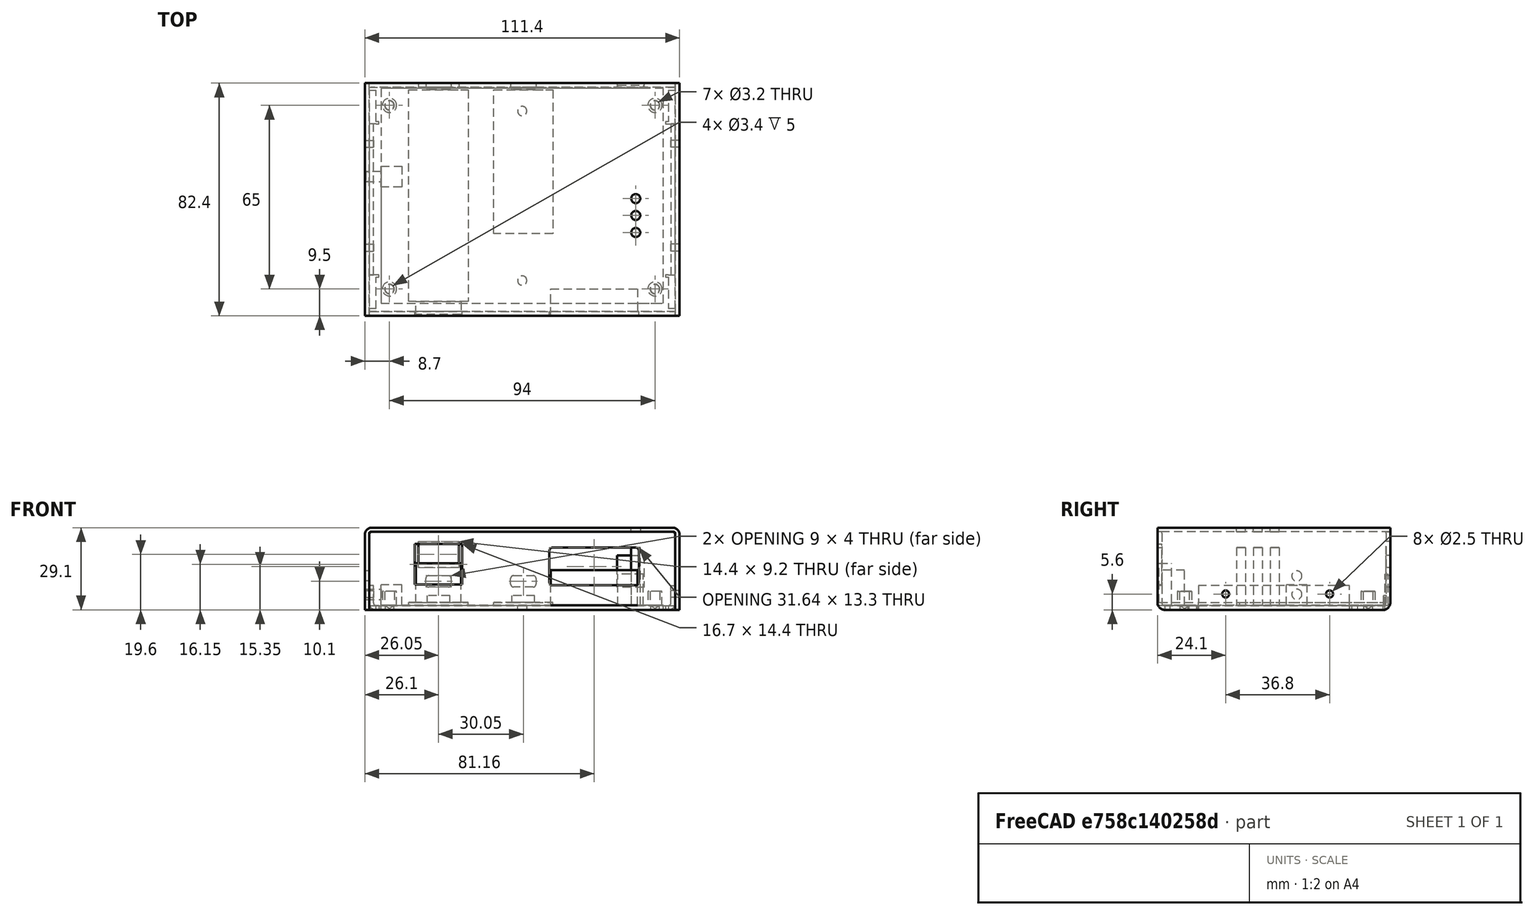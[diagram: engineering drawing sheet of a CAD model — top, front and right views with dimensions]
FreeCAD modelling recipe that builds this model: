
FCSTD DOCUMENT  (FreeCAD 0.21R33110 (Git))
Label: winners-case-v2-front
License: All rights reserved
LicenseURL: http://en.wikipedia.org/wiki/All_rights_reserved
objects: Sketcher::SketchObject×23, TechDraw::DrawViewPart×17, PartDesign::Pad×14, PartDesign::FeaturePython×6, PartDesign::Hole×6, TechDraw::DrawSVGTemplate×6, TechDraw::DrawPage×6, PartDesign::Fillet×4, TechDraw::DrawViewDimension×4, PartDesign::Body×3, App::Part×3, PartDesign::Pocket×3, Spreadsheet::Sheet×1
note: 94 computed .brp shape members not serialized (recipe doc carries the construction recipe); baked Part::Feature solids carry a one-line shape summary decoded from their .brp

FEATURE [Sketcher::SketchObject] Sketch
  FullyConstrained = true
  MapMode = 5
  Support = -> [XY_Plane]
  expr: .Constraints.pcb_h = <<fig>>.pcb_h
  expr: .Constraints.pcb_hole_bottom = <<fig>>.pcb_hole_bottom
  expr: .Constraints.pcb_hole_left = <<fig>>.pcb_hole_left
  expr: .Constraints.pcb_hole_r = <<fig>>.pcb_hole_r
  expr: .Constraints.pcb_hole_right = <<fig>>.pcb_hole_right
  expr: .Constraints.pcb_hole_top = <<fig>>.pcb_hole_top
  expr: .Constraints.pcb_w = <<fig>>.pcb_w
  sketch-geometry (9):
    g0: LineSegment StartX=50 StartY=-38 StartZ=0 EndX=50 EndY=38 EndZ=0
    g1: LineSegment StartX=50 StartY=38 StartZ=0 EndX=-50 EndY=38 EndZ=0
    g2: LineSegment StartX=-50 StartY=38 StartZ=0 EndX=-50 EndY=-38 EndZ=0
    g3: LineSegment StartX=-50 StartY=-38 StartZ=0 EndX=50 EndY=-38 EndZ=0
    g4: GeomPoint X=0 Y=0 Z=0
    g5: Circle CenterX=-47 CenterY=32 CenterZ=0 NormalX=0 NormalY=0 NormalZ=1 AngleXU=0 Radius=1.6
    g6: Circle CenterX=47 CenterY=32 CenterZ=0 NormalX=0 NormalY=0 NormalZ=1 AngleXU=0 Radius=1.6
    g7: Circle CenterX=-47 CenterY=-33 CenterZ=0 NormalX=0 NormalY=0 NormalZ=1 AngleXU=0 Radius=1.6
    g8: Circle CenterX=47 CenterY=-33 CenterZ=0 NormalX=0 NormalY=0 NormalZ=1 AngleXU=0 Radius=1.6
  constraints (24):
    c: Coincident(g0,g1)
    c: Coincident(g1,g2)
    c: Coincident(g2,g3)
    c: Coincident(g3,g0)
    c: Horizontal(g1)
    c: Horizontal(g3)
    c: Vertical(g0)
    c: Vertical(g2)
    c: Symmetric(g1,g0,g4)
    c: Coincident(g4,g-1)
    c: DistanceX(g1,g1) = 100  'pcb_w'
    c: DistanceY(g0,g0) = 76  'pcb_h'
    c: Radius(g5) = 1.6  'pcb_hole_r'
    c: Equal(g5,g6)
    c: Equal(g6,g8)
    c: Equal(g8,g7)
    c: DistanceX(g1,g5) = 3  'pcb_hole_left'
    c: DistanceY(g5,g1) = 6  'pcb_hole_top'
    c: DistanceX(g6,g0) = 3  'pcb_hole_right'
    c: DistanceY(g2,g7) = 5  'pcb_hole_bottom'
    c: Horizontal(g6,g5)
    c: Vertical(g5,g7)
    c: Vertical(g6,g8)
    c: Horizontal(g7,g8)
FEATURE [Spreadsheet::Sheet] Spreadsheet  label="fig"
  cells = A1=margin2; B1(margin2)=0.2; A2=margin; B2(margin)=0.4; A3=pcb_surface_z; B3(pcb_surface_z)==sheet_thk + standoff_h + pcb_thk; A4=pcb_w; B4(pcb_w)=100; A5=pcb_w2; B5(pcb_w2)=50; A6=pcb_h; B6(pcb_h)=76; A7=pcb_h2; B7(pcb_h2)==76 / 2; A8=pcb_thk; B8(pcb_thk)=1.6; A9=pcb_hole_left; B9(pcb_hole_left)=3; A10=pcb_hole_right; B10(pcb_hole_right)=3; A11=pcb_hole_top; B11(pcb_hole_top)=6; A12=pcb_hole_bottom; B12(pcb_hole_bottom)=5; A13=pcb_hole_r; B13(pcb_hole_r)=1.6; A14=standoff_h; B14(standoff_h)=5; A15=standoff_tab_r; B15(standoff_tab_r)=1.6; A16=standoff_r; B16(standoff_r)=2.5; A17=rj45_w; B17(rj45_w)=15.9; A18=rj45_h; B18(rj45_h)=13.6; A19=rj45_bottom_margin; B19(rj45_bottom_margin)=0.25; A20=rj45_y_ext; B20(rj45_y_ext)=4.5; A21=w5500_top; B21(w5500_top)=0.48; A22=w5500_left; B22(w5500_left)=9.85; A23=w5500_h; B23(w5500_h)=75; A24=w5500_w; B24(w5500_w)=21; A25=w5500_thk; B25(w5500_thk)=1; A26=pico_left; B26(pico_left)=39.9; A27=pico_h; B27(pico_h)=51; A28=pico_w; B28(pico_w)=21; A29=usb_w; B29(usb_w)=8; A30=usb_h; B30(usb_h)=3; A31=usb_bottom_margin; B31(usb_bottom_margin)=-0.5; A32=usb_margin; B32(usb_margin)=0.5; A33=usb_ext; B33(usb_ext)=1; A34=db9_w; B34(db9_w)=30.84; A35=db9_h; B35(db9_h)=12.5; A36=db9_support_to_face; B36(db9_support_to_face)=9.52; A37=db9_support_dist; B37(db9_support_dist)=25; A38=db9_support_to_side; B38(db9_support_to_side)=2.92; A39=db9_left; B39(db9_left)=62.96; A40=db9_bottom; B40(db9_bottom)=5.07; A41=db9_right; B41(db9_right)=12.14; A42=barrel_w; B42(barrel_w)=9; A43=barrel_h; B43(barrel_h)=11; A44=barrel_ext; B44(barrel_ext)=1.1; A45=barrel_bottom_margin; B45(barrel_bottom_margin)=-0.2; A46=barrel_support_to_face; B46(barrel_support_to_face)=0; A47=barrel_right; B47(barrel_right)=7.15; A48=pb_h; B48(pb_h)=7.4; A49=pb_w; B49(pb_w)=7.4; A50=pb_tall; B50(pb_tall)=7.2; A51=pb_r; B51(pb_r)==3.6 / 2; A52=pb_center_y; B52(pb_center_y)=31.2; A53=pb_top; B53(pb_top)==pb_center_y - pb_h / 2; A54=pb_ext; B54(pb_ext)=5.4; A55=pb_bottom_margin; B55(pb_bottom_margin)=0.3; A56=led_r; B56(led_r)==3.2 / 2; A57=led1_bottom; B57(led1_bottom)=37; A58=led2_bottom; B58(led2_bottom)=31; A59=led3_bottom; B59(led3_bottom)=25; A60=led_right; B60(led_right)=9.8; A61=led_tall; B61(led_tall)=20.5; A62=led_dist; B62(led_dist)=6; A63=sheet_thk; B63(sheet_thk)=1.5; A64=sheet_base_w2; B64(sheet_base_w2)==pcb_w2 + pb_ext - sheet_thk * 0.8; A65=sheet_h2_top; B65(sheet_h2_top)==pcb_h2 + margin; A66=sheet_h2_bottom; B66(sheet_h2_bottom)==pcb_h2 + rj45_y_ext - sheet_thk; A67=sheet_bend_tall; B67(sheet_bend_tall)==sheet_thk + standoff_h + pcb_thk + led_tall - sheet_thk + sheet_bend_add; A68=sheet_bend_add; B68(sheet_bend_add)=2; A69=sheet_wing2wall; B69(sheet_wing2wall)=12; A70=sheet_wing_h; B70(sheet_wing_h)==sheet_thk + pcb_thk + standoff_h; A71=sheet_wing_hole_top; B71(sheet_wing_hole_top)=2.5; A72=sheetwing_hole_dist; B72(sheet_wing_hole_left)=18.4; A73=rsw_w; B73(rsw_w)=14.4; A74=rsw_h; B74(rsw_h)=9.2; A75=sheetwing_hole_top; B75(sheetwing_hole_top)=2.5; A76=sheet_wing_hole_dist; B76(sheet_wing_hole_dist)=18.4; A77=sheettop_bend_tall; B77(sheettop_bend_tall)==sheet_bend_tall - sheet_bend_add - 0.5; A78=sheet_dinrail_hole_dist; B78(sheet_dinrail_hole_dist)=30
FEATURE [PartDesign::Pad] Pad  label="pcb"
  Direction = (0,0,1)
  Length = 1.6
  Length2 = 10
  Profile = -> Sketch
  ReferenceAxis = -> Sketch [N_Axis]
  Type = 0
  expr: Length = <<fig>>.pcb_thk
FEATURE [Sketcher::SketchObject] Sketch001
  AttachmentOffset = pos=(0,0,1.6) rot=(0,0,1;0rad)
  FullyConstrained = true
  MapMode = 5
  Placement = pos=(0,0,1.6) rot=(0,0,1;0rad)
  Support = -> [XY_Plane]
  expr: .AttachmentOffset.Base.z = <<fig>>.pcb_thk
  expr: .Constraints.w5500_h = <<fig>>.w5500_h
  expr: Constraints[10] = <<fig>>.pcb_w / 2 - <<fig>>.w5500_left
  expr: Constraints[11] = <<fig>>.pcb_h / 2 - 0.48
  expr: Constraints[8] = <<fig>>.w5500_w
  sketch-geometry (4):
    g0: LineSegment StartX=-40.15 StartY=37.52 StartZ=0 EndX=-19.15 EndY=37.52 EndZ=0
    g1: LineSegment StartX=-19.15 StartY=37.52 StartZ=0 EndX=-19.15 EndY=-37.48 EndZ=0
    g2: LineSegment StartX=-19.15 StartY=-37.48 StartZ=0 EndX=-40.15 EndY=-37.48 EndZ=0
    g3: LineSegment StartX=-40.15 StartY=-37.48 StartZ=0 EndX=-40.15 EndY=37.52 EndZ=0
  constraints (12):
    c: Coincident(g0,g1)
    c: Coincident(g1,g2)
    c: Coincident(g2,g3)
    c: Coincident(g3,g0)
    c: Horizontal(g0)
    c: Horizontal(g2)
    c: Vertical(g1)
    c: Vertical(g3)
    c: DistanceX(g2,g2) = 21
    c: DistanceY(g1,g1) = 75  'w5500_h'
    c: DistanceX(g0,g-1) = 40.15
    c: DistanceY(g-1,g0) = 37.52
FEATURE [PartDesign::Pad] Pad001  label="w5500-pcb"
  BaseFeature = -> Pad
  Direction = (0,0,1)
  Length = 1
  Length2 = 10
  Profile = -> Sketch001
  ReferenceAxis = -> Sketch001 [N_Axis]
  Type = 0
  expr: Length = <<fig>>.w5500_thk
FEATURE [Sketcher::SketchObject] Sketch002
  AttachmentOffset = pos=(0,0,2.59) rot=(0,0,1;0rad)
  FullyConstrained = true
  MapMode = 5
  Placement = pos=(0,0,2.59) rot=(0,0,1;0rad)
  Support = -> [XY_Plane]
  expr: .AttachmentOffset.Base.z = <<fig>>.pcb_thk + <<fig>>.w5500_thk - 0.01
  expr: .Constraints.rj45_w = <<fig>>.rj45_w
  expr: Constraints[10] = <<fig>>.w5500_top + <<fig>>.w5500_h - <<fig>>.pcb_h / 2
  expr: Constraints[11] = <<fig>>.pcb_w / 2 - <<fig>>.w5500_left - <<fig>>.w5500_w + (<<fig>>.w5500_w - <<fig>>.rj45_w) / 2
  expr: Constraints[9] = <<fig>>.rj45_y_ext
  sketch-geometry (4):
    g0: LineSegment StartX=-37.6 StartY=-37.48 StartZ=0 EndX=-21.7 EndY=-37.48 EndZ=0
    g1: LineSegment StartX=-21.7 StartY=-37.48 StartZ=0 EndX=-21.7 EndY=-41.98 EndZ=0
    g2: LineSegment StartX=-21.7 StartY=-41.98 StartZ=0 EndX=-37.6 EndY=-41.98 EndZ=0
    g3: LineSegment StartX=-37.6 StartY=-41.98 StartZ=0 EndX=-37.6 EndY=-37.48 EndZ=0
  constraints (12):
    c: Coincident(g0,g1)
    c: Coincident(g1,g2)
    c: Coincident(g2,g3)
    c: Coincident(g3,g0)
    c: Horizontal(g0)
    c: Horizontal(g2)
    c: Vertical(g1)
    c: Vertical(g3)
    c: DistanceX(g0,g0) = 15.9  'rj45_w'
    c: DistanceY(g1,g1) = 4.5
    c: DistanceY(g0,g-1) = 37.48
    c: DistanceX(g0,g-1) = 21.7
FEATURE [PartDesign::Pad] Pad002  label="w5500-rj45"
  BaseFeature = -> Pad001
  Direction = (0,0,1)
  Length = 13.85
  Length2 = 10
  Profile = -> Sketch002
  ReferenceAxis = -> Sketch002 [N_Axis]
  Type = 0
  expr: Length = <<fig>>.rj45_bottom_margin + <<fig>>.rj45_h
FEATURE [Sketcher::SketchObject] Sketch003
  AttachmentOffset = pos=(0,0,2.599) rot=(0,0,1;0rad)
  FullyConstrained = true
  MapMode = 5
  Placement = pos=(0,0,2.599) rot=(0,0,1;0rad)
  Support = -> [XY_Plane]
  expr: .AttachmentOffset.Base.z = <<fig>>.pcb_thk + <<fig>>.w5500_thk - 0.001
  expr: Constraints[10] = <<fig>>.pcb_w / 2 - <<fig>>.w5500_left - (<<fig>>.w5500_w - <<fig>>.usb_w) / 2
  expr: Constraints[11] = <<fig>>.pcb_h / 2 - <<fig>>.w5500_top
  expr: Constraints[8] = <<fig>>.usb_ext
  expr: Constraints[9] = <<fig>>.usb_w
  sketch-geometry (4):
    g0: LineSegment StartX=-33.65 StartY=38.52 StartZ=0 EndX=-25.65 EndY=38.52 EndZ=0
    g1: LineSegment StartX=-25.65 StartY=38.52 StartZ=0 EndX=-25.65 EndY=37.52 EndZ=0
    g2: LineSegment StartX=-25.65 StartY=37.52 StartZ=0 EndX=-33.65 EndY=37.52 EndZ=0
    g3: LineSegment StartX=-33.65 StartY=37.52 StartZ=0 EndX=-33.65 EndY=38.52 EndZ=0
  constraints (12):
    c: Coincident(g0,g1)
    c: Coincident(g1,g2)
    c: Coincident(g2,g3)
    c: Coincident(g3,g0)
    c: Horizontal(g0)
    c: Horizontal(g2)
    c: Vertical(g1)
    c: Vertical(g3)
    c: DistanceY(g1,g1) = 1
    c: DistanceX(g2,g2) = 8
    c: DistanceX(g2,g-1) = 33.65
    c: DistanceY(g-1,g1) = 37.52
FEATURE [PartDesign::Pad] Pad003  label="w5500-usb"
  BaseFeature = -> Pad002
  Direction = (0,0,1)
  Length = 2.5
  Length2 = 10
  Profile = -> Sketch003
  ReferenceAxis = -> Sketch003 [N_Axis]
  Type = 0
  expr: Length = <<fig>>.usb_bottom_margin + <<fig>>.usb_h
FEATURE [Sketcher::SketchObject] Sketch004
  AttachmentOffset = pos=(0,0,1.6) rot=(0,0,1;0rad)
  FullyConstrained = true
  MapMode = 5
  Placement = pos=(0,0,1.6) rot=(0,0,1;0rad)
  Support = -> [XY_Plane]
  expr: .AttachmentOffset.Base.z = <<fig>>.pcb_thk
  expr: Constraints[10] = <<fig>>.db9_left - <<fig>>.db9_support_to_side - <<fig>>.pcb_w / 2
  expr: Constraints[11] = <<fig>>.pcb_h / 2 - <<fig>>.db9_bottom
  expr: Constraints[8] = <<fig>>.db9_w
  expr: Constraints[9] = <<fig>>.db9_support_to_face
  sketch-geometry (4):
    g0: LineSegment StartX=10.04 StartY=-32.93 StartZ=0 EndX=40.88 EndY=-32.93 EndZ=0
    g1: LineSegment StartX=40.88 StartY=-32.93 StartZ=0 EndX=40.88 EndY=-42.45 EndZ=0
    g2: LineSegment StartX=40.88 StartY=-42.45 StartZ=0 EndX=10.04 EndY=-42.45 EndZ=0
    g3: LineSegment StartX=10.04 StartY=-42.45 StartZ=0 EndX=10.04 EndY=-32.93 EndZ=0
  constraints (12):
    c: Coincident(g0,g1)
    c: Coincident(g1,g2)
    c: Coincident(g2,g3)
    c: Coincident(g3,g0)
    c: Horizontal(g0)
    c: Horizontal(g2)
    c: Vertical(g1)
    c: Vertical(g3)
    c: DistanceX(g0,g0) = 30.84
    c: DistanceY(g3,g3) = 9.52
    c: DistanceX(g-1,g0) = 10.04
    c: DistanceY(g0,g-1) = 32.93
FEATURE [PartDesign::Pad] Pad004  label="DB9"
  BaseFeature = -> Pad003
  Direction = (0,0,1)
  Length = 12.5
  Length2 = 10
  Profile = -> Sketch004
  ReferenceAxis = -> Sketch004 [N_Axis]
  Type = 0
  expr: Length = <<fig>>.db9_h
FEATURE [Sketcher::SketchObject] Sketch005
  AttachmentOffset = pos=(0,0,1.6) rot=(0,0,1;0rad)
  FullyConstrained = true
  MapMode = 5
  Placement = pos=(0,0,1.6) rot=(0,0,1;0rad)
  Support = -> [XY_Plane]
  expr: .AttachmentOffset.Base.z = <<fig>>.pcb_thk
  expr: Constraints[10] = <<fig>>.pcb_h / 2 - <<fig>>.w5500_top
  expr: Constraints[11] = <<fig>>.pcb_w / 2 - <<fig>>.pico_left
  expr: Constraints[8] = <<fig>>.pico_w
  expr: Constraints[9] = <<fig>>.pico_h
  sketch-geometry (4):
    g0: LineSegment StartX=-10.1 StartY=37.52 StartZ=0 EndX=10.9 EndY=37.52 EndZ=0
    g1: LineSegment StartX=10.9 StartY=37.52 StartZ=0 EndX=10.9 EndY=-13.48 EndZ=0
    g2: LineSegment StartX=10.9 StartY=-13.48 StartZ=0 EndX=-10.1 EndY=-13.48 EndZ=0
    g3: LineSegment StartX=-10.1 StartY=-13.48 StartZ=0 EndX=-10.1 EndY=37.52 EndZ=0
  constraints (12):
    c: Coincident(g0,g1)
    c: Coincident(g1,g2)
    c: Coincident(g2,g3)
    c: Coincident(g3,g0)
    c: Horizontal(g0)
    c: Horizontal(g2)
    c: Vertical(g1)
    c: Vertical(g3)
    c: DistanceX(g0,g0) = 21
    c: DistanceY(g3,g3) = 51
    c: DistanceY(g-1,g0) = 37.52
    c: DistanceX(g0,g-1) = 10.1
FEATURE [PartDesign::Pad] Pad005  label="pico-pcb"
  BaseFeature = -> Pad004
  Direction = (0,0,1)
  Length = 1
  Length2 = 10
  Profile = -> Sketch005
  ReferenceAxis = -> Sketch005 [N_Axis]
  Type = 0
  expr: Length = <<fig>>.w5500_thk
FEATURE [Sketcher::SketchObject] Sketch006
  AttachmentOffset = pos=(0,0,2.599) rot=(0,0,1;0rad)
  FullyConstrained = true
  MapMode = 5
  Placement = pos=(0,0,2.599) rot=(0,0,1;0rad)
  Support = -> [XY_Plane]
  expr: .AttachmentOffset.Base.z = <<fig>>.pcb_thk + <<fig>>.w5500_thk - 0.001
  expr: Constraints[10] = <<fig>>.pcb_w / 2 - <<fig>>.pico_left - (<<fig>>.pico_w - <<fig>>.usb_w) / 2
  expr: Constraints[11] = <<fig>>.pcb_h / 2 - <<fig>>.w5500_top
  expr: Constraints[8] = <<fig>>.usb_w
  expr: Constraints[9] = <<fig>>.usb_ext
  sketch-geometry (4):
    g0: LineSegment StartX=-3.6 StartY=38.52 StartZ=0 EndX=4.4 EndY=38.52 EndZ=0
    g1: LineSegment StartX=4.4 StartY=38.52 StartZ=0 EndX=4.4 EndY=37.52 EndZ=0
    g2: LineSegment StartX=4.4 StartY=37.52 StartZ=0 EndX=-3.6 EndY=37.52 EndZ=0
    g3: LineSegment StartX=-3.6 StartY=37.52 StartZ=0 EndX=-3.6 EndY=38.52 EndZ=0
  constraints (12):
    c: Coincident(g0,g1)
    c: Coincident(g1,g2)
    c: Coincident(g2,g3)
    c: Coincident(g3,g0)
    c: Horizontal(g0)
    c: Horizontal(g2)
    c: Vertical(g1)
    c: Vertical(g3)
    c: DistanceX(g0,g0) = 8
    c: DistanceY(g1,g1) = 1
    c: DistanceX(g2,g-1) = 3.6
    c: DistanceY(g-1,g2) = 37.52
FEATURE [PartDesign::Pad] Pad006  label="pico-usb"
  BaseFeature = -> Pad005
  Direction = (0,0,1)
  Length = 2.5
  Length2 = 10
  Profile = -> Sketch006
  ReferenceAxis = -> Sketch006 [N_Axis]
  Type = 0
  expr: Length = <<fig>>.usb_bottom_margin + <<fig>>.usb_h
FEATURE [Sketcher::SketchObject] Sketch007
  AttachmentOffset = pos=(0,0,1.599) rot=(0,0,1;0rad)
  FullyConstrained = true
  MapMode = 5
  Placement = pos=(0,0,1.599) rot=(0,0,1;0rad)
  Support = -> [XY_Plane]
  expr: .AttachmentOffset.Base.z = <<fig>>.pcb_thk - 0.001
  expr: Constraints[10] = <<fig>>.pcb_w / 2 - <<fig>>.barrel_right - <<fig>>.barrel_w
  expr: Constraints[11] = <<fig>>.pcb_h / 2
  expr: Constraints[8] = <<fig>>.barrel_w
  expr: Constraints[9] = <<fig>>.barrel_ext
  sketch-geometry (4):
    g0: LineSegment StartX=33.85 StartY=39.1 StartZ=0 EndX=42.85 EndY=39.1 EndZ=0
    g1: LineSegment StartX=42.85 StartY=39.1 StartZ=0 EndX=42.85 EndY=38 EndZ=0
    g2: LineSegment StartX=42.85 StartY=38 StartZ=0 EndX=33.85 EndY=38 EndZ=0
    g3: LineSegment StartX=33.85 StartY=38 StartZ=0 EndX=33.85 EndY=39.1 EndZ=0
  constraints (12):
    c: Coincident(g0,g1)
    c: Coincident(g1,g2)
    c: Coincident(g2,g3)
    c: Coincident(g3,g0)
    c: Horizontal(g0)
    c: Horizontal(g2)
    c: Vertical(g1)
    c: Vertical(g3)
    c: DistanceX(g0,g0) = 9
    c: DistanceY(g3,g3) = 1.1
    c: DistanceX(g-1,g2) = 33.85
    c: DistanceY(g-1,g2) = 38
FEATURE [PartDesign::Pad] Pad007  label="barrel-jack"
  BaseFeature = -> Pad006
  Direction = (0,0,1)
  Length = 11
  Length2 = 10
  Profile = -> Sketch007
  ReferenceAxis = -> Sketch007 [N_Axis]
  Type = 0
  expr: Length = <<fig>>.barrel_h
FEATURE [Sketcher::SketchObject] Sketch008
  AttachmentOffset = pos=(0,0,1.6) rot=(0,0,1;0rad)
  FullyConstrained = true
  MapMode = 5
  Placement = pos=(0,0,1.6) rot=(0,0,1;0rad)
  Support = -> [XY_Plane]
  expr: .AttachmentOffset.Base.z = <<fig>>.pcb_thk
  expr: Constraints[10] = <<fig>>.pcb_h / 2 - <<fig>>.pb_top
  expr: Constraints[11] = <<fig>>.pcb_w / 2
  expr: Constraints[8] = <<fig>>.pb_w
  expr: Constraints[9] = <<fig>>.pb_h
  sketch-geometry (4):
    g0: LineSegment StartX=-50 StartY=10.5 StartZ=0 EndX=-42.6 EndY=10.5 EndZ=0
    g1: LineSegment StartX=-42.6 StartY=10.5 StartZ=0 EndX=-42.6 EndY=3.1 EndZ=0
    g2: LineSegment StartX=-42.6 StartY=3.1 StartZ=0 EndX=-50 EndY=3.1 EndZ=0
    g3: LineSegment StartX=-50 StartY=3.1 StartZ=0 EndX=-50 EndY=10.5 EndZ=0
  constraints (12):
    c: Coincident(g0,g1)
    c: Coincident(g1,g2)
    c: Coincident(g2,g3)
    c: Coincident(g3,g0)
    c: Horizontal(g0)
    c: Horizontal(g2)
    c: Vertical(g1)
    c: Vertical(g3)
    c: DistanceX(g0,g0) = 7.4
    c: DistanceY(g3,g3) = 7.4
    c: DistanceY(g-1,g0) = 10.5
    c: DistanceX(g2,g-1) = 50
FEATURE [PartDesign::Pad] Pad008  label="push-button"
  BaseFeature = -> Pad007
  Direction = (0,0,1)
  Length = 7.2
  Length2 = 10
  Profile = -> Sketch008
  ReferenceAxis = -> Sketch008 [N_Axis]
  Type = 0
  expr: Length = <<fig>>.pb_tall
FEATURE [Sketcher::SketchObject] Sketch009
  AttachmentOffset = pos=(0,0,-50) rot=(0,0,1;0rad)
  FullyConstrained = true
  MapMode = 5
  Placement = pos=(-50,1.11e-14,-1.11e-14) rot=(0.57735,0.57735,0.57735;2.0944rad)
  Support = -> [YZ_Plane]
  expr: .AttachmentOffset.Base.z = -<<fig>>.pcb_w2
  expr: Constraints[0] = <<fig>>.pb_r
  expr: Constraints[1] = <<fig>>.pcb_thk + <<fig>>.pb_tall / 2 + <<fig>>.pb_bottom_margin
  expr: Constraints[2] = <<fig>>.pcb_h2 - <<fig>>.pb_top - <<fig>>.pb_h / 2
  sketch-geometry (1):
    g0: Circle CenterX=6.8 CenterY=5.5 CenterZ=0 NormalX=0 NormalY=0 NormalZ=1 AngleXU=0 Radius=1.8
  constraints (3):
    c: Radius(g0) = 1.8
    c: DistanceY(g-1,g0) = 5.5
    c: DistanceX(g-1,g0) = 6.8
FEATURE [PartDesign::Pad] Pad009
  BaseFeature = -> Pad008
  Direction = (1,-2e-16,3e-16)
  Length = 5.4
  Length2 = 10
  Profile = -> Sketch009
  ReferenceAxis = -> Sketch009 [N_Axis]
  Reversed = true
  Type = 0
  expr: Length = <<fig>>.pb_ext
FEATURE [Sketcher::SketchObject] Sketch010
  AttachmentOffset = pos=(0,0,1.6) rot=(0,0,1;0rad)
  FullyConstrained = true
  MapMode = 5
  Placement = pos=(0,0,1.6) rot=(0,0,1;0rad)
  Support = -> [XY_Plane]
  expr: .AttachmentOffset.Base.z = <<fig>>.pcb_thk
  expr: Constraints[0] = <<fig>>.led_r
  expr: Constraints[3] = <<fig>>.pcb_w2 - <<fig>>.led_right
  expr: Constraints[6] = <<fig>>.pcb_h2 - <<fig>>.led1_bottom
  expr: Constraints[7] = <<fig>>.led_dist
  expr: Constraints[8] = <<fig>>.led_dist
  sketch-geometry (3):
    g0: Circle CenterX=40.2 CenterY=-1 CenterZ=0 NormalX=0 NormalY=0 NormalZ=1 AngleXU=0 Radius=1.6
    g1: Circle CenterX=40.2 CenterY=-7 CenterZ=0 NormalX=0 NormalY=0 NormalZ=1 AngleXU=0 Radius=1.6
    g2: Circle CenterX=40.2 CenterY=-13 CenterZ=0 NormalX=0 NormalY=0 NormalZ=1 AngleXU=0 Radius=1.6
  constraints (9):
    c: Radius(g0) = 1.6
    c: Equal(g0,g1)
    c: Equal(g1,g2)
    c: DistanceX(g-1,g0) = 40.2
    c: Vertical(g0,g1)
    c: Vertical(g1,g2)
    c: DistanceY(g0,g-1) = 1
    c: DistanceY(g1,g0) = 6
    c: DistanceY(g2,g1) = 6
FEATURE [PartDesign::Pad] Pad010
  BaseFeature = -> Pad009
  Direction = (0,0,1)
  Length = 20.5
  Length2 = 10
  Profile = -> Sketch010
  ReferenceAxis = -> Sketch010 [N_Axis]
  Type = 0
  expr: Length = <<fig>>.led_tall
FEATURE [PartDesign::Body] Body
  Group = -> [Sketch,Pad,Sketch001,Pad001,Sketch002,Pad002,Sketch003,Pad003,Sketch004,Pad004,Sketch005,Pad005,Sketch006,Pad006,Sketch007,Pad007,Sketch008,Pad008,Sketch009,Pad009,Sketch010,Pad010]
  Origin = -> Origin
  Tip = -> Pad010
FEATURE [App::Part] Part001  label="pcb2"
  Group = -> [Body]
  Origin = -> Origin002
  Placement = pos=(0,0,6.5) rot=(0,0,1;0rad)
  expr: .Placement.Base.z = <<fig>>.sheet_thk + <<fig>>.standoff_h
FEATURE [Sketcher::SketchObject] Sketch011
  FullyConstrained = true
  MapMode = 5
  Support = -> [XY_Plane004]
  expr: Constraints[10] = <<fig>>.pcb_h2 + <<fig>>.rj45_y_ext - <<fig>>.sheet_thk
  expr: Constraints[8] = <<fig>>.sheet_base_w2
  expr: Constraints[9] = <<fig>>.pcb_h2 + <<fig>>.margin
  sketch-geometry (5):
    g0: LineSegment StartX=54.2 StartY=-41 StartZ=0 EndX=54.2 EndY=38.4 EndZ=0
    g1: LineSegment StartX=54.2 StartY=38.4 StartZ=0 EndX=-54.2 EndY=38.4 EndZ=0
    g2: LineSegment StartX=-54.2 StartY=38.4 StartZ=0 EndX=-54.2 EndY=-41 EndZ=0
    g3: LineSegment StartX=-54.2 StartY=-41 StartZ=0 EndX=54.2 EndY=-41 EndZ=0
    g4: GeomPoint X=0 Y=0 Z=0
  constraints (12):
    c: Coincident(g0,g1)
    c: Coincident(g1,g2)
    c: Coincident(g2,g3)
    c: Coincident(g3,g0)
    c: Horizontal(g1)
    c: Vertical(g0)
    c: Vertical(g2)
    c: Coincident(g4,g-1)
    c: DistanceX(g1,g4) = 54.2
    c: DistanceY(g4,g1) = 38.4
    c: DistanceY(g2,g4) = 41
    c: Symmetric(g2,g0,g-2)
FEATURE [PartDesign::Pad] Pad011  label="base"
  Direction = (0,0,1)
  Length = 1.5
  Length2 = 10
  Profile = -> Sketch011
  ReferenceAxis = -> Sketch011 [N_Axis]
  Type = 0
  expr: Length = <<fig>>.sheet_thk
FEATURE [PartDesign::FeaturePython] Bend  # WARN: FeaturePython — macro-defined, semantics opaque (R4)
  AutoMiter = true
  BaseFeature = -> Pad011
  BendType = 2
  LengthList = [25.1]
  LengthSpec = 0
  ReliefFactor = 0.7
  UseReliefFactor = false
  angle = 90
  baseObject = -> Pad011 [Edge7]
  bendAList = [90]
  extend1 = 0
  extend2 = 0
  gap1 = 0
  gap2 = 0
  invert = true
  kfactor = 0.5
  length = 25.1
  maxExtendDist = 5
  minGap = 0.1
  minReliefGap = 1
  miterangle1 = 0
  miterangle2 = 0
  offset = 0
  radius = 1
  reliefType = 0
  reliefd = 1
  reliefw = 0.8
  sketchflip = false
  sketchinvert = false
  unfold = false
FEATURE [PartDesign::FeaturePython] Bend001  # WARN: FeaturePython — macro-defined, semantics opaque (R4)
  AutoMiter = true
  BaseFeature = -> Bend
  BendType = 2
  LengthList = [25.1]
  LengthSpec = 0
  ReliefFactor = 0.7
  UseReliefFactor = false
  angle = 90
  baseObject = -> Bend [Edge24]
  bendAList = [90]
  extend1 = 0
  extend2 = 0
  gap1 = 0
  gap2 = 0
  invert = true
  kfactor = 0.5
  length = 25.1
  maxExtendDist = 5
  minGap = 0.1
  minReliefGap = 1
  miterangle1 = 0
  miterangle2 = 0
  offset = 0
  radius = 1
  reliefType = 0
  reliefd = 1
  reliefw = 0.8
  sketchflip = false
  sketchinvert = false
  unfold = false
  expr: length = <<fig>>.sheet_thk + <<fig>>.standoff_h + <<fig>>.pcb_thk + <<fig>>.led_tall - <<fig>>.sheet_thk - <<fig>>.sheet_bend_add
FEATURE [Sketcher::SketchObject] Sketch012
  AttachmentOffset = pos=(0,0,44) rot=(0,0,1;0rad)
  FullyConstrained = true
  MapMode = 5
  Placement = pos=(0,-44,-9.8e-15) rot=(1,0,0;1.5708rad)
  Support = -> [XZ_Plane004]
  expr: .AttachmentOffset.Base.z = <<fig>>.pcb_h2 + <<fig>>.rj45_y_ext + <<fig>>.sheet_thk
  expr: Constraints[18] = <<fig>>.sheet_thk + <<fig>>.standoff_h + <<fig>>.pcb_thk + <<fig>>.w5500_thk - <<fig>>.margin
  expr: Constraints[19] = <<fig>>.db9_h + <<fig>>.margin * 2
  expr: Constraints[20] = <<fig>>.db9_w + <<fig>>.margin * 2
  expr: Constraints[21] = <<fig>>.db9_left - <<fig>>.db9_support_to_side - <<fig>>.pcb_w / 2 - <<fig>>.margin
  expr: Constraints[22] = <<fig>>.rj45_w + <<fig>>.margin * 2
  expr: Constraints[23] = <<fig>>.rj45_h + <<fig>>.margin * 2
  expr: Constraints[24] = <<fig>>.sheet_thk + <<fig>>.standoff_h + <<fig>>.pcb_thk + <<fig>>.rj45_bottom_margin + <<fig>>.w5500_thk - <<fig>>.margin
  expr: Constraints[25] = <<fig>>.pcb_w / 2 - <<fig>>.w5500_left - <<fig>>.w5500_w + (<<fig>>.w5500_w - <<fig>>.rj45_w) / 2 - <<fig>>.margin
  sketch-geometry (10):
    g0: LineSegment StartX=9.64 StartY=22 StartZ=0 EndX=9.64 EndY=8.7 EndZ=0
    g1: LineSegment StartX=9.64 StartY=8.7 StartZ=0 EndX=41.28 EndY=8.7 EndZ=0
    g2: LineSegment StartX=41.28 StartY=8.7 StartZ=0 EndX=41.28 EndY=22 EndZ=0
    g3: LineSegment StartX=41.28 StartY=22 StartZ=0 EndX=9.64 EndY=22 EndZ=0
    g4: GeomPoint X=25.46 Y=15.35 Z=0
    g5: LineSegment StartX=-38 StartY=23.35 StartZ=0 EndX=-38 EndY=8.95 EndZ=0
    g6: LineSegment StartX=-38 StartY=8.95 StartZ=0 EndX=-21.3 EndY=8.95 EndZ=0
    g7: LineSegment StartX=-21.3 StartY=8.95 StartZ=0 EndX=-21.3 EndY=23.35 EndZ=0
    g8: LineSegment StartX=-21.3 StartY=23.35 StartZ=0 EndX=-38 EndY=23.35 EndZ=0
    g9: GeomPoint X=-29.65 Y=16.15 Z=0
  constraints (26):
    c: Coincident(g0,g1)
    c: Coincident(g1,g2)
    c: Coincident(g2,g3)
    c: Coincident(g3,g0)
    c: Horizontal(g1)
    c: Horizontal(g3)
    c: Vertical(g0)
    c: Vertical(g2)
    c: Symmetric(g1,g0,g4)
    c: Coincident(g5,g6)
    c: Coincident(g6,g7)
    c: Coincident(g7,g8)
    c: Coincident(g8,g5)
    c: Horizontal(g6)
    c: Horizontal(g8)
    c: Vertical(g5)
    c: Vertical(g7)
    c: Symmetric(g6,g5,g9)
    c: DistanceY(g-1,g0) = 8.7
    c: DistanceY(g0,g0) = 13.3
    c: DistanceX(g3,g3) = 31.64
    c: DistanceX(g-1,g0) = 9.64
    c: DistanceX(g6,g6) = 16.7
    c: DistanceY(g7,g7) = 14.4
    c: DistanceY(g-1,g6) = 8.95
    c: DistanceX(g6,g-1) = 21.3
FEATURE [PartDesign::Pocket] Pocket
  BaseFeature = -> Bend001
  Direction = (0,1,2e-16)
  Length = 5
  Length2 = 5
  Profile = -> Sketch012
  ReferenceAxis = -> Sketch012 [N_Axis]
  Type = 0
FEATURE [Sketcher::SketchObject] Sketch013
  AttachmentOffset = pos=(0,0,-39.9) rot=(0,0,1;0rad)
  FullyConstrained = true
  MapMode = 5
  Placement = pos=(0,39.9,8.9e-15) rot=(1,0,0;1.5708rad)
  Support = -> [XZ_Plane004]
  expr: .AttachmentOffset.Base.z = -<<fig>>.pcb_h2 - <<fig>>.sheet_thk - <<fig>>.margin
  expr: Constraints[32] = <<fig>>.barrel_w + <<fig>>.margin2 * 2
  expr: Constraints[33] = <<fig>>.barrel_h + <<fig>>.margin2 * 2
  expr: Constraints[34] = <<fig>>.sheet_thk + <<fig>>.standoff_h + <<fig>>.pcb_thk - <<fig>>.margin2
  expr: Constraints[35] = <<fig>>.pcb_w2 - <<fig>>.barrel_w - <<fig>>.barrel_right - <<fig>>.margin2
  expr: Constraints[36] = <<fig>>.usb_w + <<fig>>.usb_margin * 2
  expr: Constraints[37] = <<fig>>.usb_h + <<fig>>.usb_margin * 2
  expr: Constraints[38] = <<fig>>.pcb_surface_z + <<fig>>.w5500_thk + <<fig>>.usb_bottom_margin - <<fig>>.usb_margin
  expr: Constraints[39] = <<fig>>.pcb_w / 2 - <<fig>>.pico_left - (<<fig>>.pico_w - <<fig>>.usb_w) / 2 + <<fig>>.usb_margin
  expr: Constraints[40] = <<fig>>.pcb_w / 2 - <<fig>>.w5500_left - (<<fig>>.w5500_w - <<fig>>.usb_w) / 2 + <<fig>>.usb_margin
  expr: Constraints[41] = <<fig>>.rsw_w
  expr: Constraints[42] = <<fig>>.rsw_h
  sketch-geometry (16):
    g0: LineSegment StartX=33.65 StartY=19.3 StartZ=0 EndX=43.05 EndY=19.3 EndZ=0
    g1: LineSegment StartX=43.05 StartY=19.3 StartZ=0 EndX=43.05 EndY=7.9 EndZ=0
    g2: LineSegment StartX=43.05 StartY=7.9 StartZ=0 EndX=33.65 EndY=7.9 EndZ=0
    g3: LineSegment StartX=33.65 StartY=7.9 StartZ=0 EndX=33.65 EndY=19.3 EndZ=0
    g4: LineSegment StartX=-4.1 StartY=12.1 StartZ=0 EndX=4.9 EndY=12.1 EndZ=0
    g5: LineSegment StartX=4.9 StartY=12.1 StartZ=0 EndX=4.9 EndY=8.1 EndZ=0
    g6: LineSegment StartX=4.9 StartY=8.1 StartZ=0 EndX=-4.1 EndY=8.1 EndZ=0
    g7: LineSegment StartX=-4.1 StartY=8.1 StartZ=0 EndX=-4.1 EndY=12.1 EndZ=0
    g8: LineSegment StartX=-34.15 StartY=12.1 StartZ=0 EndX=-25.15 EndY=12.1 EndZ=0
    g9: LineSegment StartX=-25.15 StartY=12.1 StartZ=0 EndX=-25.15 EndY=8.1 EndZ=0
    g10: LineSegment StartX=-25.15 StartY=8.1 StartZ=0 EndX=-34.15 EndY=8.1 EndZ=0
    g11: LineSegment StartX=-34.15 StartY=8.1 StartZ=0 EndX=-34.15 EndY=12.1 EndZ=0
    g12: LineSegment StartX=-36.8 StartY=24.2 StartZ=0 EndX=-22.4 EndY=24.2 EndZ=0
    g13: LineSegment StartX=-22.4 StartY=24.2 StartZ=0 EndX=-22.4 EndY=15 EndZ=0
    g14: LineSegment StartX=-22.4 StartY=15 StartZ=0 EndX=-36.8 EndY=15 EndZ=0
    g15: LineSegment StartX=-36.8 StartY=15 StartZ=0 EndX=-36.8 EndY=24.2 EndZ=0
  constraints (48):
    c: Coincident(g0,g1)
    c: Coincident(g1,g2)
    c: Coincident(g2,g3)
    c: Coincident(g3,g0)
    c: Horizontal(g0)
    c: Horizontal(g2)
    c: Vertical(g1)
    c: Vertical(g3)
    c: Coincident(g4,g5)
    c: Coincident(g5,g6)
    c: Coincident(g6,g7)
    c: Coincident(g7,g4)
    c: Horizontal(g4)
    c: Horizontal(g6)
    c: Vertical(g5)
    c: Vertical(g7)
    c: Coincident(g8,g9)
    c: Coincident(g9,g10)
    c: Coincident(g10,g11)
    c: Coincident(g11,g8)
    c: Horizontal(g8)
    c: Horizontal(g10)
    c: Vertical(g9)
    c: Vertical(g11)
    c: Coincident(g12,g13)
    c: Coincident(g13,g14)
    c: Coincident(g14,g15)
    c: Coincident(g15,g12)
    c: Horizontal(g12)
    c: Horizontal(g14)
    c: Vertical(g13)
    c: Vertical(g15)
    c: DistanceX(g2,g2) = 9.4
    c: DistanceY(g3,g3) = 11.4
    c: DistanceY(g-1,g2) = 7.9
    c: DistanceX(g-1,g2) = 33.65
    c: DistanceX(g6,g6) = 9
    c: DistanceY(g5,g5) = 4
    c: DistanceY(g-1,g5) = 8.1
    c: DistanceX(g6,g-1) = 4.1
    c: DistanceX(g10,g-1) = 34.15
    c: DistanceX(g12,g12) = 14.4
    c: DistanceY(g13,g13) = 9.2
    c: DistanceX(g13,g-1) = 22.4
    c: DistanceY(g-1,g13) = 15
    c: Equal(g7,g9)
    c: Equal(g4,g8)
    c: Horizontal(g6,g9)
FEATURE [PartDesign::Pocket] Pocket001
  BaseFeature = -> Pocket
  Direction = (0,1,2e-16)
  Length = 1.5
  Length2 = 5
  Profile = -> Sketch013
  ReferenceAxis = -> Sketch013 [N_Axis]
  Reversed = true
  Type = 0
  expr: Length = <<fig>>.sheet_thk
FEATURE [PartDesign::FeaturePython] Bend002  label="bend_wing_left"  # WARN: FeaturePython — macro-defined, semantics opaque (R4)
  AutoMiter = true
  BaseFeature = -> Pocket001
  BendType = 1
  LengthList = [6.1]
  LengthSpec = 0
  ReliefFactor = 0.7
  UseReliefFactor = false
  angle = 90
  baseObject = -> Pocket001 [Edge36]
  bendAList = [90]
  extend1 = 0
  extend2 = 0
  gap1 = 12
  gap2 = 12
  invert = true
  kfactor = 0.5
  length = 6.1
  maxExtendDist = 5
  minGap = 0.1
  minReliefGap = 1
  miterangle1 = 0
  miterangle2 = 0
  offset = 0
  radius = 1
  reliefType = 0
  reliefd = 1
  reliefw = 0.8
  sketchflip = false
  sketchinvert = false
  unfold = false
  expr: gap1 = <<fig>>.sheet_wing2wall
  expr: gap2 = <<fig>>.sheet_wing2wall
  expr: length = <<fig>>.sheet_wing_h - <<fig>>.sheet_bend_add
FEATURE [Sketcher::SketchObject] Sketch014
  AttachmentOffset = pos=(0,0,-54.2) rot=(0,0,1;0rad)
  FullyConstrained = true
  MapMode = 5
  Placement = pos=(-54.2,1.2e-14,-1.2e-14) rot=(0.57735,0.57735,0.57735;2.0944rad)
  Support = -> [YZ_Plane004]
  expr: .AttachmentOffset.Base.z = -<<fig>>.sheet_base_w2
  expr: Constraints[0] = <<fig>>.sheet_wing_h - <<fig>>.sheet_wing_hole_top
  expr: Constraints[2] = <<fig>>.sheet_wing_hole_dist
  expr: Constraints[3] = <<fig>>.sheet_wing_hole_dist
  sketch-geometry (2):
    g0: Circle CenterX=-18.4 CenterY=5.6 CenterZ=0 NormalX=0 NormalY=0 NormalZ=1 AngleXU=0 Radius=1.6
    g1: Circle CenterX=18.4 CenterY=5.6 CenterZ=0 NormalX=0 NormalY=0 NormalZ=1 AngleXU=0 Radius=1.6
  constraints (6):
    c: DistanceY(g-1,g0) = 5.6
    c: Horizontal(g0,g1)
    c: DistanceX(g0,g-1) = 18.4
    c: DistanceX(g-1,g1) = 18.4
    c: Radius(g0) = 1.6
    c: Equal(g0,g1)
FEATURE [PartDesign::Hole] Hole
  BaseFeature = -> Bend002
  CustomThreadClearance = 0
  Depth = 25
  DepthType = 0
  Diameter = 2.5
  DrillForDepth = false
  DrillPoint = 1
  DrillPointAngle = 118
  HoleCutCountersinkAngle = 90
  HoleCutCustomValues = false
  HoleCutDepth = 0
  HoleCutDiameter = 6.1
  HoleCutType = 0
  ModelThread = false
  Profile = -> Sketch014
  Reversed = true
  Tapered = false
  TaperedAngle = 90
  ThreadClass = 0
  ThreadDepth = 25
  ThreadDepthType = 0
  ThreadDirection = 0
  ThreadFit = 0
  ThreadSize = 9
  ThreadType = 1
  Threaded = true
  UseCustomThreadClearance = false
FEATURE [PartDesign::FeaturePython] Bend003  # WARN: FeaturePython — macro-defined, semantics opaque (R4)
  AutoMiter = true
  BaseFeature = -> Hole
  BendType = 1
  LengthList = [6.1]
  LengthSpec = 0
  ReliefFactor = 0.7
  UseReliefFactor = false
  angle = 90
  baseObject = -> Hole [Edge31]
  bendAList = [90]
  extend1 = 0
  extend2 = 0
  gap1 = 12
  gap2 = 12
  invert = true
  kfactor = 0.5
  length = 6.1
  maxExtendDist = 5
  minGap = 0.1
  minReliefGap = 1
  miterangle1 = 0
  miterangle2 = 0
  offset = 0
  radius = 1
  reliefType = 0
  reliefd = 1
  reliefw = 0.8
  sketchflip = false
  sketchinvert = false
  unfold = false
  expr: gap1 = <<fig>>.sheet_wing2wall
  expr: gap2 = <<fig>>.sheet_wing2wall
  expr: length = <<fig>>.sheet_wing_h - <<fig>>.sheet_bend_add
FEATURE [Sketcher::SketchObject] Sketch015
  AttachmentOffset = pos=(0,0,54.2) rot=(0,0,1;0rad)
  FullyConstrained = true
  MapMode = 5
  Placement = pos=(54.2,-1.2e-14,1.2e-14) rot=(0.57735,0.57735,0.57735;2.0944rad)
  Support = -> [YZ_Plane004]
  expr: .AttachmentOffset.Base.z = <<fig>>.sheet_base_w2
  expr: Constraints[0] = <<fig>>.sheet_wing_h - <<fig>>.sheet_wing_hole_top
  expr: Constraints[1] = <<fig>>.sheet_wing_hole_dist
  expr: Constraints[5] = <<fig>>.sheet_wing_hole_dist
  sketch-geometry (2):
    g0: Circle CenterX=-18.4 CenterY=5.6 CenterZ=0 NormalX=0 NormalY=0 NormalZ=1 AngleXU=0 Radius=1.6
    g1: Circle CenterX=18.4 CenterY=5.6 CenterZ=0 NormalX=0 NormalY=0 NormalZ=1 AngleXU=0 Radius=1.6
  constraints (6):
    c: DistanceY(g-1,g0) = 5.6
    c: DistanceX(g0,g-1) = 18.4
    c: Radius(g0) = 1.6
    c: Equal(g0,g1)
    c: Horizontal(g1,g0)
    c: DistanceX(g-1,g1) = 18.4
FEATURE [PartDesign::Hole] Hole001
  BaseFeature = -> Bend003
  CustomThreadClearance = 0
  Depth = 25
  DepthType = 0
  Diameter = 2.5
  DrillForDepth = false
  DrillPoint = 1
  DrillPointAngle = 118
  HoleCutCountersinkAngle = 90
  HoleCutCustomValues = false
  HoleCutDepth = 0
  HoleCutDiameter = 6.1
  HoleCutType = 0
  ModelThread = false
  Profile = -> Sketch015
  Tapered = false
  TaperedAngle = 90
  ThreadClass = 0
  ThreadDepth = 25
  ThreadDepthType = 0
  ThreadDirection = 0
  ThreadFit = 0
  ThreadSize = 9
  ThreadType = 1
  Threaded = true
  UseCustomThreadClearance = false
FEATURE [Sketcher::SketchObject] Sketch016
  AttachmentOffset = pos=(0,0,29.1) rot=(0,0,1;0rad)
  FullyConstrained = true
  MapMode = 5
  Placement = pos=(0,0,29.1) rot=(0,0,1;0rad)
  Support = -> [XY_Plane006]
  expr: .AttachmentOffset.Base.z = <<fig>>.sheet_bend_tall
  expr: Constraints[10] = <<fig>>.sheet_h2_top + <<fig>>.sheet_thk
  expr: Constraints[11] = <<fig>>.sheet_h2_bottom + <<fig>>.sheet_thk
  expr: Constraints[12] = <<fig>>.led_r
  expr: Constraints[14] = <<fig>>.pcb_w2 - <<fig>>.led_right
  expr: Constraints[17] = <<fig>>.led_dist
  expr: Constraints[18] = <<fig>>.led_dist
  expr: Constraints[19] = <<fig>>.pcb_h2 - <<fig>>.led1_bottom
  expr: Constraints[8] = <<fig>>.sheet_base_w2
  expr: Constraints[9] = <<fig>>.sheet_base_w2
  sketch-geometry (7):
    g0: LineSegment StartX=-54.2 StartY=39.9 StartZ=0 EndX=54.2 EndY=39.9 EndZ=0
    g1: LineSegment StartX=54.2 StartY=39.9 StartZ=0 EndX=54.2 EndY=-42.5 EndZ=0
    g2: LineSegment StartX=54.2 StartY=-42.5 StartZ=0 EndX=-54.2 EndY=-42.5 EndZ=0
    g3: LineSegment StartX=-54.2 StartY=-42.5 StartZ=0 EndX=-54.2 EndY=39.9 EndZ=0
    g4: Circle CenterX=40.2 CenterY=-1 CenterZ=0 NormalX=0 NormalY=0 NormalZ=1 AngleXU=0 Radius=1.6
    g5: Circle CenterX=40.2 CenterY=-13 CenterZ=0 NormalX=0 NormalY=0 NormalZ=1 AngleXU=0 Radius=1.6
    g6: Circle CenterX=40.2 CenterY=-7 CenterZ=0 NormalX=0 NormalY=0 NormalZ=1 AngleXU=0 Radius=1.6
  constraints (21):
    c: Coincident(g0,g1)
    c: Coincident(g1,g2)
    c: Coincident(g2,g3)
    c: Coincident(g3,g0)
    c: Horizontal(g0)
    c: Horizontal(g2)
    c: Vertical(g1)
    c: Vertical(g3)
    c: DistanceX(g0,g-1) = 54.2
    c: DistanceX(g-1,g0) = 54.2
    c: DistanceY(g-1,g0) = 39.9
    c: DistanceY(g1,g-1) = 42.5
    c: Radius(g4) = 1.6
    c: Equal(g4,g6)
    c: DistanceX(g-1,g4) = 40.2
    c: Vertical(g4,g6)
    c: Vertical(g6,g5)
    c: DistanceY(g6,g4) = 6
    c: DistanceY(g5,g6) = 6
    c: DistanceY(g4,g-1) = 1
    c: Equal(g5,g6)
FEATURE [PartDesign::Pad] Pad012
  Direction = (0,0,1)
  Length = 1.5
  Length2 = 10
  Profile = -> Sketch016
  ReferenceAxis = -> Sketch016 [N_Axis]
  Reversed = true
  Type = 0
  expr: Length = <<fig>>.sheet_thk
FEATURE [PartDesign::FeaturePython] Bend004  # WARN: FeaturePython — macro-defined, semantics opaque (R4)
  AutoMiter = true
  BaseFeature = -> Pad012
  BendType = 2
  LengthList = [26.6]
  LengthSpec = 0
  ReliefFactor = 0.7
  UseReliefFactor = false
  angle = 90
  baseObject = -> Pad012 [Edge7]
  bendAList = [90]
  extend1 = 0
  extend2 = 0
  gap1 = 0
  gap2 = 0
  invert = true
  kfactor = 0.5
  length = 26.6
  maxExtendDist = 5
  minGap = 0.1
  minReliefGap = 1
  miterangle1 = 0
  miterangle2 = 0
  offset = 0
  radius = 1
  reliefType = 0
  reliefd = 1
  reliefw = 0.8
  sketchflip = false
  sketchinvert = false
  unfold = false
  expr: length = <<fig>>.sheet_bend_tall - <<fig>>.sheet_bend_add - 0.5
FEATURE [Sketcher::SketchObject] Sketch017
  AttachmentOffset = pos=(0,0,55.7) rot=(0,0,1;0rad)
  FullyConstrained = true
  MapMode = 5
  Placement = pos=(55.7,-1.24e-14,1.24e-14) rot=(0.57735,0.57735,0.57735;2.0944rad)
  Support = -> [YZ_Plane006]
  expr: .AttachmentOffset.Base.z = <<fig>>.sheet_base_w2 + <<fig>>.sheet_thk
  expr: Constraints[0] = <<fig>>.sheet_wing_hole_dist
  expr: Constraints[1] = <<fig>>.sheet_wing_hole_dist
  expr: Constraints[2] = <<fig>>.sheet_wing_h - <<fig>>.sheet_wing_hole_top
  expr: Constraints[4] = 1.6
  sketch-geometry (2):
    g0: Circle CenterX=-18.4 CenterY=5.6 CenterZ=0 NormalX=0 NormalY=0 NormalZ=1 AngleXU=0 Radius=1.35133
    g1: Circle CenterX=18.4 CenterY=5.6 CenterZ=0 NormalX=0 NormalY=0 NormalZ=1 AngleXU=0 Radius=1.35133
  constraints (6):
    c: DistanceX(g0,g-1) = 18.4
    c: DistanceX(g-1,g1) = 18.4
    c: DistanceY(g-1,g0) = 5.6
    c: Horizontal(g0,g1)
    c: Radius(g0) = 1.35133
    c: Equal(g1,g0)
FEATURE [PartDesign::Hole] Hole002
  BaseFeature = -> Bend004
  CustomThreadClearance = 0
  Depth = 1.5
  DepthType = 0
  Diameter = 2.5
  DrillForDepth = false
  DrillPoint = 1
  DrillPointAngle = 118
  HoleCutCountersinkAngle = 90
  HoleCutCustomValues = false
  HoleCutDepth = 0
  HoleCutDiameter = 6.1
  HoleCutType = 0
  ModelThread = false
  Profile = -> Sketch017
  Tapered = false
  TaperedAngle = 90
  ThreadClass = 0
  ThreadDepth = 1.5
  ThreadDepthType = 0
  ThreadDirection = 0
  ThreadFit = 0
  ThreadSize = 9
  ThreadType = 1
  Threaded = true
  UseCustomThreadClearance = false
  expr: Depth = <<fig>>.sheet_thk
FEATURE [PartDesign::FeaturePython] Bend005  # WARN: FeaturePython — macro-defined, semantics opaque (R4)
  AutoMiter = true
  BaseFeature = -> Hole002
  BendType = 2
  LengthList = [26.6]
  LengthSpec = 0
  ReliefFactor = 0.7
  UseReliefFactor = false
  angle = 90
  baseObject = -> Hole002 [Edge31]
  bendAList = [90]
  extend1 = 0
  extend2 = 0
  gap1 = 0
  gap2 = 0
  invert = true
  kfactor = 0.5
  length = 26.6
  maxExtendDist = 5
  minGap = 0.1
  minReliefGap = 1
  miterangle1 = 0
  miterangle2 = 0
  offset = 0
  radius = 1
  reliefType = 0
  reliefd = 1
  reliefw = 0.8
  sketchflip = false
  sketchinvert = false
  unfold = false
  expr: length = <<fig>>.sheet_bend_tall - <<fig>>.sheet_bend_add - 0.5
FEATURE [Sketcher::SketchObject] Sketch018
  AttachmentOffset = pos=(0,0,-55.7) rot=(0,0,1;0rad)
  FullyConstrained = true
  MapMode = 5
  Placement = pos=(-55.7,1.24e-14,-1.24e-14) rot=(0.57735,0.57735,0.57735;2.0944rad)
  Support = -> [YZ_Plane006]
  expr: .AttachmentOffset.Base.z = -(<<fig>>.sheet_base_w2 + <<fig>>.sheet_thk)
  expr: Constraints[0] = <<fig>>.sheet_wing_hole_dist
  expr: Constraints[1] = <<fig>>.sheet_wing_hole_dist
  expr: Constraints[2] = <<fig>>.sheet_wing_h - <<fig>>.sheet_wing_hole_top
  sketch-geometry (2):
    g0: Circle CenterX=-18.4 CenterY=5.6 CenterZ=0 NormalX=0 NormalY=0 NormalZ=1 AngleXU=0 Radius=1.6
    g1: Circle CenterX=18.4 CenterY=5.6 CenterZ=0 NormalX=0 NormalY=0 NormalZ=1 AngleXU=0 Radius=1.6
  constraints (6):
    c: DistanceX(g0,g-1) = 18.4
    c: DistanceX(g-1,g1) = 18.4
    c: DistanceY(g-1,g0) = 5.6
    c: Horizontal(g0,g1)
    c: Radius(g0) = 1.6
    c: Equal(g0,g1)
FEATURE [PartDesign::Hole] Hole003
  BaseFeature = -> Bend005
  CustomThreadClearance = 0
  Depth = 1.5
  DepthType = 0
  Diameter = 2.5
  DrillForDepth = false
  DrillPoint = 1
  DrillPointAngle = 118
  HoleCutCountersinkAngle = 90
  HoleCutCustomValues = false
  HoleCutDepth = 0
  HoleCutDiameter = 6.1
  HoleCutType = 0
  ModelThread = false
  Profile = -> Sketch018
  Reversed = true
  Tapered = false
  TaperedAngle = 90
  ThreadClass = 0
  ThreadDepth = 1.5
  ThreadDepthType = 0
  ThreadDirection = 0
  ThreadFit = 0
  ThreadSize = 9
  ThreadType = 1
  Threaded = true
  UseCustomThreadClearance = false
  expr: Depth = <<fig>>.sheet_thk
FEATURE [PartDesign::Fillet] Fillet
  Base = -> Hole001 [Edge213,Edge216,Edge214,Edge215]
  BaseFeature = -> Hole001
  Radius = 1
  SupportTransform = false
  UseAllEdges = false
FEATURE [PartDesign::Fillet] Fillet001
  Base = -> Fillet [Edge184,Edge192,Edge188,Edge196,Edge186,Edge194,Edge191,Edge183]
  BaseFeature = -> Fillet
  Radius = 1
  SupportTransform = false
  UseAllEdges = false
FEATURE [Sketcher::SketchObject] Sketch019
  AttachmentOffset = pos=(0,0,1.5) rot=(0,0,1;0rad)
  FullyConstrained = true
  MapMode = 5
  Placement = pos=(0,0,1.5) rot=(0,0,1;0rad)
  Support = -> [XY_Plane004]
  expr: .AttachmentOffset.Base.z = <<fig>>.sheet_thk
  expr: Constraints[0] = <<fig>>.pcb_w2 - <<fig>>.pcb_hole_left
  expr: Constraints[10] = <<fig>>.pcb_h2 - <<fig>>.pcb_hole_bottom
  expr: Constraints[1] = <<fig>>.pcb_w2 - <<fig>>.pcb_hole_right
  expr: Constraints[2] = <<fig>>.pcb_h2 - <<fig>>.pcb_hole_top
  expr: Constraints[3] = <<fig>>.standoff_r
  sketch-geometry (4):
    g0: Circle CenterX=-47 CenterY=32 CenterZ=0 NormalX=0 NormalY=0 NormalZ=1 AngleXU=0 Radius=2.5
    g1: Circle CenterX=47 CenterY=32 CenterZ=0 NormalX=0 NormalY=0 NormalZ=1 AngleXU=0 Radius=2.5
    g2: Circle CenterX=-47 CenterY=-33 CenterZ=0 NormalX=0 NormalY=0 NormalZ=1 AngleXU=0 Radius=2.5
    g3: Circle CenterX=47 CenterY=-33 CenterZ=0 NormalX=0 NormalY=0 NormalZ=1 AngleXU=0 Radius=2.5
  constraints (12):
    c: DistanceX(g0,g-1) = 47
    c: DistanceX(g-1,g1) = 47
    c: DistanceY(g-1,g0) = 32
    c: Radius(g0) = 2.5
    c: Equal(g3,g0)
    c: Equal(g0,g1)
    c: Equal(g1,g2)
    c: Horizontal(g0,g1)
    c: Vertical(g2,g0)
    c: Vertical(g1,g3)
    c: DistanceY(g2,g-1) = 33
    c: Horizontal(g2,g3)
FEATURE [PartDesign::Pad] Pad013
  BaseFeature = -> Fillet001
  Direction = (0,0,1)
  Length = 5
  Length2 = 10
  Profile = -> Sketch019
  ReferenceAxis = -> Sketch019 [N_Axis]
  Type = 0
  expr: Length = <<fig>>.standoff_h
FEATURE [Sketcher::SketchObject] Sketch020
  AttachmentOffset = pos=(0,0,6.5) rot=(0,0,1;0rad)
  FullyConstrained = true
  MapMode = 5
  Placement = pos=(0,0,6.5) rot=(0,0,1;0rad)
  Support = -> [XY_Plane004]
  expr: .AttachmentOffset.Base.z = <<fig>>.sheet_thk + <<fig>>.standoff_h
  expr: Constraints[0] = <<fig>>.pcb_hole_r
  expr: Constraints[11] = <<fig>>.pcb_h2 - <<fig>>.pcb_hole_top
  expr: Constraints[1] = <<fig>>.pcb_w2 - <<fig>>.pcb_hole_left
  expr: Constraints[2] = <<fig>>.pcb_w2 - <<fig>>.pcb_hole_right
  expr: Constraints[3] = <<fig>>.pcb_h2 - <<fig>>.pcb_hole_bottom
  sketch-geometry (4):
    g0: Circle CenterX=-47 CenterY=32 CenterZ=0 NormalX=0 NormalY=0 NormalZ=1 AngleXU=0 Radius=1.6
    g1: Circle CenterX=47 CenterY=32 CenterZ=0 NormalX=0 NormalY=0 NormalZ=1 AngleXU=0 Radius=1.6
    g2: Circle CenterX=-47 CenterY=-33 CenterZ=0 NormalX=0 NormalY=0 NormalZ=1 AngleXU=0 Radius=1.6
    g3: Circle CenterX=47 CenterY=-33 CenterZ=0 NormalX=0 NormalY=0 NormalZ=1 AngleXU=0 Radius=1.6
  constraints (12):
    c: Radius(g0) = 1.6
    c: DistanceX(g0,g-1) = 47
    c: DistanceX(g-1,g1) = 47
    c: DistanceY(g2,g-1) = 33
    c: Equal(g0,g1)
    c: Equal(g1,g3)
    c: Equal(g3,g2)
    c: Horizontal(g0,g1)
    c: Horizontal(g2,g3)
    c: Vertical(g0,g2)
    c: Vertical(g1,g3)
    c: DistanceY(g-1,g0) = 32
FEATURE [PartDesign::Hole] Hole004
  BaseFeature = -> Pad013
  CustomThreadClearance = 0
  Depth = 5
  DepthType = 0
  Diameter = 3.4
  DrillForDepth = false
  DrillPoint = 1
  DrillPointAngle = 118
  HoleCutCountersinkAngle = 90
  HoleCutCustomValues = false
  HoleCutDepth = 0
  HoleCutDiameter = 6.1
  HoleCutType = 0
  ModelThread = false
  Profile = -> Sketch020
  Tapered = false
  TaperedAngle = 90
  ThreadClass = 0
  ThreadDepth = 5
  ThreadDepthType = 0
  ThreadDirection = 0
  ThreadFit = 0
  ThreadSize = 9
  ThreadType = 1
  Threaded = false
  UseCustomThreadClearance = false
FEATURE [PartDesign::Fillet] Fillet002
  Base = -> Hole004 [Edge244,Edge246,Edge50,Edge54]
  BaseFeature = -> Hole004
  Radius = 0.5
  SupportTransform = false
  UseAllEdges = false
FEATURE [PartDesign::Fillet] Fillet003
  Base = -> Hole003 [Edge8,Edge63,Edge51,Edge2]
  BaseFeature = -> Hole003
  Radius = 2.5
  SupportTransform = false
  UseAllEdges = false
FEATURE [TechDraw::DrawSVGTemplate] Template
  Height = 210
  Orientation = 1
  Width = 297
FEATURE [TechDraw::DrawSVGTemplate] Template001
  Height = 210
  Orientation = 1
  Width = 297
FEATURE [Sketcher::SketchObject] Sketch021
  FullyConstrained = true
  MapMode = 5
  Support = -> [XY_Plane004]
  expr: Constraints[2] = <<fig>>.sheet_dinrail_hole_dist
  expr: Constraints[3] = <<fig>>.sheet_dinrail_hole_dist
  sketch-geometry (2):
    g0: Circle CenterX=0 CenterY=30 CenterZ=0 NormalX=0 NormalY=0 NormalZ=1 AngleXU=0 Radius=1.65
    g1: Circle CenterX=0 CenterY=-30 CenterZ=0 NormalX=0 NormalY=0 NormalZ=1 AngleXU=0 Radius=1.65
  constraints (6):
    c: Vertical(g0,g1)
    c: Vertical(g1,g-1)
    c: DistanceY(g-1,g0) = 30
    c: DistanceY(g1,g-1) = 30
    c: Diameter(g0) = 3.3
    c: Equal(g0,g1)
FEATURE [PartDesign::Hole] Hole005
  BaseFeature = -> Fillet002
  CustomThreadClearance = 0
  Depth = 1.5
  DepthType = 0
  Diameter = 3.3
  DrillForDepth = false
  DrillPoint = 1
  DrillPointAngle = 118
  HoleCutCountersinkAngle = 90
  HoleCutCustomValues = false
  HoleCutDepth = 0
  HoleCutDiameter = 6.1
  HoleCutType = 0
  ModelThread = false
  Profile = -> Sketch021
  Reversed = true
  Tapered = false
  TaperedAngle = 90
  ThreadClass = 0
  ThreadDepth = 1.5
  ThreadDepthType = 0
  ThreadDirection = 0
  ThreadFit = 0
  ThreadSize = 11
  ThreadType = 1
  Threaded = true
  UseCustomThreadClearance = false
FEATURE [PartDesign::Body] Body001  label="base-sheet"
  Group = -> [Sketch011,Pad011,Bend,Bend001,Sketch012,Pocket,Sketch013,Pocket001,Bend002,Sketch014,Hole,Bend003,Sketch015,Hole001,Fillet,Fillet001,Sketch019,Pad013,Sketch020,Hole004,Fillet002,Sketch021,Hole005]
  Origin = -> Origin004
  Tip = -> Hole005
FEATURE [App::Part] Part  label="part-base"
  Group = -> [Body001]
  Origin = -> Origin003
FEATURE [TechDraw::DrawViewPart] View001
  CoarseView = false
  Direction = (0.61,-0.7,0.372)
  Focus = 100
  HardHidden = false
  IsoCount = 0
  IsoHidden = false
  IsoVisible = false
  LockPosition = false
  Perspective = false
  Rotation = 0
  ScaleType = 0
  ScrubCount = 0
  SeamHidden = false
  SeamVisible = true
  SmoothHidden = false
  SmoothVisible = true
  Source = -> [Body001]
  X = 146.874
  XDirection = (0.762,0.647,-0.033)
  Y = 82.9242
FEATURE [TechDraw::DrawViewPart] View002
  CoarseView = false
  Direction = (0.61,-0.7,0.372)
  Focus = 100
  HardHidden = false
  IsoCount = 0
  IsoHidden = false
  IsoVisible = false
  LockPosition = false
  Perspective = false
  Rotation = 0
  ScaleType = 0
  ScrubCount = 0
  SeamHidden = false
  SeamVisible = true
  SmoothHidden = false
  SmoothVisible = true
  Source = -> [Body001]
  X = 81.2168
  XDirection = (0.762,0.647,-0.033)
  Y = 161.532
FEATURE [TechDraw::DrawViewPart] View004
  CoarseView = false
  Direction = (0,0,1)
  Focus = 100
  HardHidden = false
  IsoCount = 0
  IsoHidden = false
  IsoVisible = false
  LockPosition = false
  Perspective = false
  Rotation = 0
  ScaleType = 0
  ScrubCount = 0
  SeamHidden = false
  SeamVisible = true
  SmoothHidden = false
  SmoothVisible = true
  Source = -> [Body001]
  X = 225.494
  XDirection = (1,0,0)
  Y = 164.133
FEATURE [TechDraw::DrawViewPart] View005
  CoarseView = false
  Direction = (0,1,0)
  Focus = 100
  HardHidden = false
  IsoCount = 0
  IsoHidden = false
  IsoVisible = false
  LockPosition = false
  Perspective = false
  Rotation = 0
  ScaleType = 0
  ScrubCount = 0
  SeamHidden = false
  SeamVisible = true
  SmoothHidden = false
  SmoothVisible = true
  Source = -> [Body001]
  X = 80.1763
  XDirection = (-1,0,0)
  Y = 38.9306
FEATURE [TechDraw::DrawViewPart] View006
  CoarseView = false
  Direction = (1,0,0)
  Focus = 100
  HardHidden = false
  IsoCount = 0
  IsoHidden = false
  IsoVisible = false
  LockPosition = false
  Perspective = false
  Rotation = 0
  ScaleType = 0
  ScrubCount = 0
  SeamHidden = false
  SeamVisible = true
  SmoothHidden = false
  SmoothVisible = true
  Source = -> [Body001]
  X = 224.974
  XDirection = (0,1,0)
  Y = 84.8844
FEATURE [TechDraw::DrawViewPart] View007
  CoarseView = false
  Direction = (-1,0,0)
  Focus = 100
  HardHidden = false
  IsoCount = 0
  IsoHidden = false
  IsoVisible = false
  LockPosition = false
  Perspective = false
  Rotation = 0
  ScaleType = 0
  ScrubCount = 0
  SeamHidden = false
  SeamVisible = true
  SmoothHidden = false
  SmoothVisible = true
  Source = -> [Body001]
  X = 224.974
  XDirection = (0,-1,0)
  Y = 37.0231
FEATURE [TechDraw::DrawViewPart] View003
  CoarseView = false
  Direction = (0,-1,0)
  Focus = 100
  HardHidden = false
  IsoCount = 0
  IsoHidden = false
  IsoVisible = false
  LockPosition = false
  Perspective = false
  Rotation = 0
  ScaleType = 0
  ScrubCount = 0
  SeamHidden = false
  SeamVisible = true
  SmoothHidden = false
  SmoothVisible = true
  Source = -> [Body001]
  X = 79.8295
  XDirection = (1,0,0)
  Y = 88.8728
FEATURE [TechDraw::DrawPage] Page001  label="base_page"
  KeepUpdated = true
  NextBalloonIndex = 1
  ProjectionType = 0
  Template = -> Template001
  Views = -> [View002,View003,View004,View005,View006,View007]
FEATURE [TechDraw::DrawSVGTemplate] Template002
  Height = 210
  Orientation = 1
  Width = 297
FEATURE [Sketcher::SketchObject] Sketch022
  AttachmentOffset = pos=(0,0,-55.7) rot=(0,0,1;0rad)
  FullyConstrained = true
  MapMode = 5
  Placement = pos=(-55.7,1.24e-14,-1.24e-14) rot=(0.57735,0.57735,0.57735;2.0944rad)
  Support = -> [YZ_Plane006]
  expr: .AttachmentOffset.Base.z = -(<<fig>>.sheet_base_w2 + <<fig>>.sheet_thk)
  expr: Constraints[1] = <<fig>>.pcb_surface_z + <<fig>>.pb_bottom_margin + <<fig>>.pb_tall / 2
  expr: Constraints[2] = <<fig>>.pcb_h2 - <<fig>>.pb_top - <<fig>>.pb_h / 2
  sketch-geometry (1):
    g0: Circle CenterX=6.8 CenterY=12 CenterZ=0 NormalX=0 NormalY=0 NormalZ=1 AngleXU=0 Radius=1.8
  constraints (3):
    c: Radius(g0) = 1.8
    c: DistanceY(g-1,g0) = 12
    c: DistanceX(g-1,g0) = 6.8
FEATURE [PartDesign::Pocket] Pocket002
  BaseFeature = -> Fillet003
  Direction = (-1,2e-16,-3e-16)
  Length = 1.5
  Length2 = 5
  Profile = -> Sketch022
  ReferenceAxis = -> Sketch022 [N_Axis]
  Reversed = true
  Type = 0
FEATURE [PartDesign::Body] Body002  label="top-sheet"
  Group = -> [Sketch016,Pad012,Bend004,Sketch017,Hole002,Bend005,Sketch018,Hole003,Fillet003,Sketch022,Pocket002]
  Origin = -> Origin006
  Tip = -> Pocket002
FEATURE [App::Part] Part002  label="part-top"
  Group = -> [Body002]
  Origin = -> Origin005
FEATURE [TechDraw::DrawViewPart] View
  CoarseView = false
  Direction = (0.61,-0.7,0.372)
  Focus = 100
  HardHidden = false
  IsoCount = 0
  IsoHidden = false
  IsoVisible = false
  LockPosition = false
  Perspective = false
  Rotation = 0
  ScaleType = 0
  ScrubCount = 0
  SeamHidden = false
  SeamVisible = true
  SmoothHidden = false
  SmoothVisible = true
  Source = -> [Body002]
  X = 151.251
  XDirection = (0.762,0.647,-0.033)
  Y = 155.526
FEATURE [TechDraw::DrawPage] Page  label="whole_page"
  KeepUpdated = true
  NextBalloonIndex = 1
  ProjectionType = 0
  Template = -> Template
  Views = -> [View,View001]
FEATURE [TechDraw::DrawViewPart] View008
  CoarseView = false
  Direction = (0.577,-0.577,0.577)
  Focus = 100
  HardHidden = false
  IsoCount = 0
  IsoHidden = false
  IsoVisible = false
  LockPosition = false
  Perspective = false
  Rotation = 0
  ScaleType = 0
  ScrubCount = 0
  SeamHidden = false
  SeamVisible = true
  SmoothHidden = false
  SmoothVisible = true
  Source = -> [Part002]
  X = 74.974
  XDirection = (0.707,0.707,0)
  Y = 154.769
FEATURE [TechDraw::DrawViewPart] View009
  CoarseView = false
  Direction = (0,0,1)
  Focus = 100
  HardHidden = false
  IsoCount = 0
  IsoHidden = false
  IsoVisible = false
  LockPosition = false
  Perspective = false
  Rotation = 0
  ScaleType = 0
  ScrubCount = 0
  SeamHidden = false
  SeamVisible = true
  SmoothHidden = false
  SmoothVisible = true
  Source = -> [Part002]
  X = 222.373
  XDirection = (1,0,0)
  Y = 65.4624
FEATURE [TechDraw::DrawViewPart] View010
  CoarseView = false
  Direction = (0,-1,0)
  Focus = 100
  HardHidden = false
  IsoCount = 0
  IsoHidden = false
  IsoVisible = false
  LockPosition = false
  Perspective = false
  Rotation = 0
  ScaleType = 0
  ScrubCount = 0
  SeamHidden = false
  SeamVisible = true
  SmoothHidden = false
  SmoothVisible = true
  Source = -> [Part002]
  X = 87.4595
  XDirection = (1,0,0)
  Y = 37.1965
FEATURE [TechDraw::DrawViewPart] View011
  CoarseView = false
  Direction = (-1,0,0)
  Focus = 100
  HardHidden = false
  IsoCount = 0
  IsoHidden = false
  IsoVisible = false
  LockPosition = false
  Perspective = false
  Rotation = 0
  ScaleType = 0
  ScrubCount = 0
  SeamHidden = false
  SeamVisible = true
  SmoothHidden = false
  SmoothVisible = true
  Source = -> [Part002]
  X = 85.3786
  XDirection = (0,-1,0)
  Y = 78.9884
FEATURE [TechDraw::DrawViewPart] View012
  CoarseView = false
  Direction = (0,0,-1)
  Focus = 100
  HardHidden = false
  IsoCount = 0
  IsoHidden = false
  IsoVisible = false
  LockPosition = false
  Perspective = false
  Rotation = 0
  ScaleType = 0
  ScrubCount = 0
  SeamHidden = false
  SeamVisible = true
  SmoothHidden = false
  SmoothVisible = true
  Source = -> [Part002]
  X = 222.546
  XDirection = (1,0,0)
  Y = 161.879
FEATURE [TechDraw::DrawPage] Page002  label="top_page"
  KeepUpdated = true
  NextBalloonIndex = 1
  ProjectionType = 0
  Template = -> Template002
  Views = -> [View008,View009,View010,View011,View012]
FEATURE [TechDraw::DrawSVGTemplate] Template003
  Height = 210
  Orientation = 1
  Template = <path>
  Width = 297
FEATURE [TechDraw::DrawViewPart] View013
  CoarseView = false
  Direction = (-0.677383,-0.682349,0.274868)
  Focus = 100
  HardHidden = false
  IsoCount = 0
  IsoHidden = false
  IsoVisible = false
  LockPosition = false
  Perspective = false
  Rotation = 0
  ScaleType = 0
  ScrubCount = 0
  SeamHidden = false
  SeamVisible = true
  SmoothHidden = false
  SmoothVisible = true
  Source = -> [Body002]
  X = 148.5
  XDirection = (0.72211,-0.688081,0.0714295)
  Y = 105
FEATURE [TechDraw::DrawPage] Page003  label="top_left_3d_page"
  KeepUpdated = true
  NextBalloonIndex = 1
  ProjectionType = 0
  Template = -> Template003
  Views = -> [View013]
FEATURE [TechDraw::DrawSVGTemplate] Template004
  Height = 210
  Orientation = 1
  Template = <path>
  Width = 297
FEATURE [TechDraw::DrawViewPart] View014
  CoarseView = false
  Direction = (0.68467,-0.704619,0.186384)
  Focus = 100
  HardHidden = false
  IsoCount = 0
  IsoHidden = false
  IsoVisible = false
  LockPosition = false
  Perspective = false
  Rotation = 0
  ScaleType = 0
  ScrubCount = 0
  SeamHidden = false
  SeamVisible = true
  SmoothHidden = false
  SmoothVisible = true
  Source = -> [Part002]
  X = 148.5
  XDirection = (0.719384,0.694393,-0.0174775)
  Y = 105
FEATURE [TechDraw::DrawPage] Page004  label="top_right_3d_page"
  KeepUpdated = true
  NextBalloonIndex = 1
  ProjectionType = 0
  Template = -> Template004
  Views = -> [View014]
FEATURE [TechDraw::DrawSVGTemplate] Template005
  Height = 210
  Orientation = 1
  Template = <path>
  Width = 297
FEATURE [TechDraw::DrawViewPart] View015  label="right"
  CoarseView = false
  Direction = (1,5.9605e-08,3.57628e-07)
  Focus = 100
  HardHidden = false
  IsoCount = 0
  IsoHidden = false
  IsoVisible = false
  LockPosition = false
  Perspective = false
  Rotation = 0
  ScaleType = 0
  ScrubCount = 0
  SeamHidden = false
  SeamVisible = true
  SmoothHidden = false
  SmoothVisible = true
  Source = -> [Part]
  X = 200.723
  XDirection = (-5.9605e-08,1,0)
  Y = 101.494
FEATURE [TechDraw::DrawViewPart] View016  label="left"
  CoarseView = false
  Direction = (-1,1.19209e-07,-1.78814e-07)
  Focus = 100
  HardHidden = false
  IsoCount = 0
  IsoHidden = false
  IsoVisible = false
  LockPosition = false
  Perspective = false
  Rotation = 0
  ScaleType = 0
  ScrubCount = 0
  SeamHidden = false
  SeamVisible = true
  SmoothHidden = false
  SmoothVisible = true
  Source = -> [Part]
  X = 88.1573
  XDirection = (-1.19209e-07,-1,1.78814e-07)
  Y = 100.387
FEATURE [TechDraw::DrawViewDimension] Dimension
  AngleOverride = false
  Arbitrary = false
  ArbitraryTolerances = false
  EqualTolerance = true
  ExtensionAngle = 0
  FormatSpec = %.2w
  FormatSpecOverTolerance = %+.2w
  FormatSpecUnderTolerance = %+.2w
  Inverted = false
  LineAngle = 0
  LockPosition = false
  MeasureType = 1
  OverTolerance = 0
  References2D = -> [View016]
  Rotation = 0
  ScaleType = 0
  TheoreticalExact = false
  Type = 1
  UnderTolerance = 0
  X = -30.9553
  Y = -16.7308
FEATURE [TechDraw::DrawViewDimension] Dimension001
  AngleOverride = false
  Arbitrary = false
  ArbitraryTolerances = false
  EqualTolerance = true
  ExtensionAngle = 0
  FormatSpec = %.2w
  FormatSpecOverTolerance = %+.2w
  FormatSpecUnderTolerance = %+.2w
  Inverted = false
  LineAngle = 0
  LockPosition = false
  MeasureType = 1
  OverTolerance = 0
  References2D = -> [View016]
  Rotation = 0
  ScaleType = 0
  TheoreticalExact = false
  Type = 1
  UnderTolerance = 0
  X = 30.7126
  Y = -16.9052
FEATURE [TechDraw::DrawViewDimension] Dimension002
  AngleOverride = false
  Arbitrary = false
  ArbitraryTolerances = false
  EqualTolerance = true
  ExtensionAngle = 0
  FormatSpec = %.2w
  FormatSpecOverTolerance = %+.2w
  FormatSpecUnderTolerance = %+.2w
  Inverted = false
  LineAngle = 0
  LockPosition = false
  MeasureType = 1
  OverTolerance = 0
  References2D = -> [View015]
  Rotation = 0
  ScaleType = 0
  TheoreticalExact = false
  Type = 1
  UnderTolerance = 0
  X = -29.3145
  Y = -18.5664
FEATURE [TechDraw::DrawViewDimension] Dimension003
  AngleOverride = false
  Arbitrary = false
  ArbitraryTolerances = false
  EqualTolerance = true
  ExtensionAngle = 0
  FormatSpec = %.2w
  FormatSpecOverTolerance = %+.2w
  FormatSpecUnderTolerance = %+.2w
  Inverted = false
  LineAngle = 0
  LockPosition = false
  MeasureType = 1
  OverTolerance = 0
  References2D = -> [View015]
  Rotation = 0
  ScaleType = 0
  TheoreticalExact = false
  Type = 1
  UnderTolerance = 0
  X = 30.121
  Y = -17.3328
FEATURE [TechDraw::DrawPage] Page005  label="base_right_left_page"
  KeepUpdated = true
  NextBalloonIndex = 1
  ProjectionType = 0
  Template = -> Template005
  Views = -> [View015,View016,Dimension,Dimension001,Dimension002,Dimension003]
note: 3 file-system paths scrubbed to <path> (originals preserved in the JSON sidecar)
